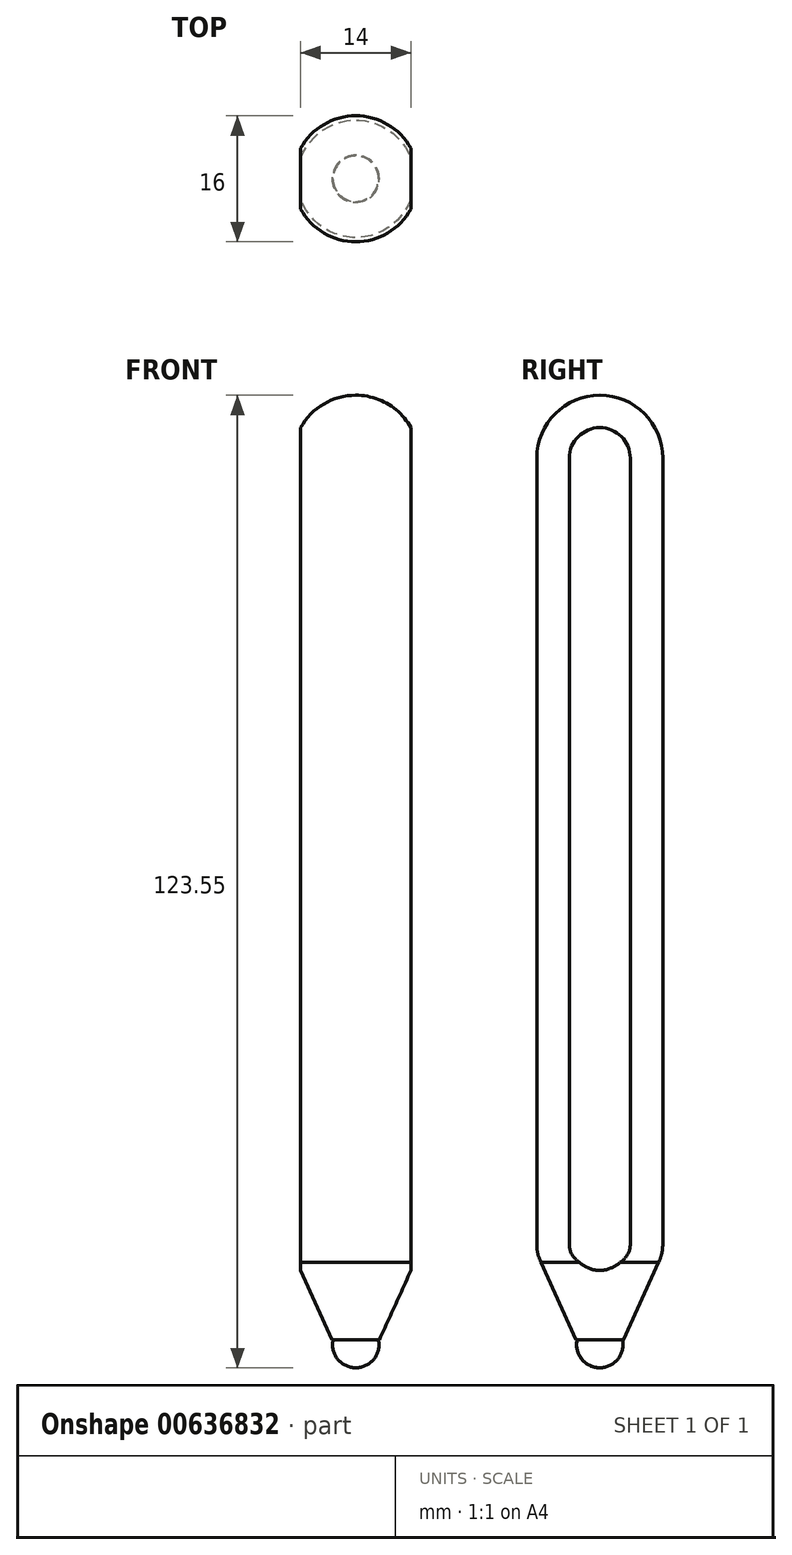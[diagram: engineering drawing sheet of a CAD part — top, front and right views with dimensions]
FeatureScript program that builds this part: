
annotation { "Feature Type Name" : "Feature", "Feature Type Description" : "" }
export const myFeature = defineFeature(function(context is Context, id is Id, definition is map)
    precondition{}
    {
        {
            var Q0;
            Q0=qCreatedBy(makeId("Top.planeOp"),FACE);
            var sketch = newSketch(context, id + "F0", { "sketchPlane" : qUnion([Q0])});
            skCircle(sketch, "E0", {"center": v(0, 0) * mm, "radius": 8 * mm});
            skSolve(sketch);
        }
        {
            var Q0;
            Q0=makeQuery(id+"F0.imprint","IMPRINT",FACE,{"disambiguationData":[TD([[makeQuery(id+"F0.imprint","IMPRINT",EDGE,{"derivedFrom":sQuery(id+"F0.wireOp",EDGE,"E0")}),1.0]])]});
            extrude(context, id + "F1", {"entities" : qUnion([Q0]), "depth" : 120 * mm, "offsetDistance" : 25 * mm});
        }
        {
            var Q0;
            Q0=makeQuery(id+"F1.opExtrude","CAP_FACE",FACE,{"disambiguationData":[OSD([sQuery(id+"F0.wireOp",EDGE,"E0")])],"isStart":false});
            fillet(context, id + "F2", {"entities" : qUnion([Q0]), "radius" : 8 * mm, "tangentPropagation" : true, "allowEdgeOverflow" : false});
        }
        {
            var Q0;
            Q0=makeQuery(id+"F1.opExtrude","CAP_FACE",FACE,{"disambiguationData":[OSD([sQuery(id+"F0.wireOp",EDGE,"E0")])],"isStart":true});
            chamfer(context, id + "F3", {"entities" : qUnion([Q0]), "chamferType" : ChamferType.TWO_OFFSETS, "width1" : 11 * mm, "oppositeDirection" : false, "width2" : 5 * mm, "tangentPropagation" : true});
        }
        {
            var Q0;
            Q0=qCreatedBy(makeId("Right.planeOp"),FACE);
            var sketch = newSketch(context, id + "F4", { "sketchPlane" : qUnion([Q0])});
            skArc(sketch, "E1", {"start": v(0, -3.55) * mm, "mid": v(2.95, -0.6) * mm, "end": v(0, 2.34) * mm});
            skLineSegment(sketch, "E2", {"start": v(0, 2.34) * mm, "end": v(0, -3.55) * mm});
            skSolve(sketch);
        }
        {
            var Q0;
            Q0=makeQuery(id+"F4.imprint","IMPRINT",FACE,{"disambiguationData":[TD([[makeQuery(id+"F4.imprint","IMPRINT",EDGE,{"derivedFrom":sQuery(id+"F4.wireOp",EDGE,"E1")}),1.0]])]});
            var Q1;
            Q1=sQuery(id+"F4.wireOp",EDGE,"E2");
            revolve(context, id + "F5", {"operationType" : NewBodyOperationType.ADD, "entities" : qUnion([Q0]), "axis" : qUnion([Q1]), "revolveType" : RevolveType.FULL});
        }
        {
            var Q0;
            Q0=qCreatedBy(makeId("Top.planeOp"),FACE);
            cPlane(context, id + "F6", {"entities" : qUnion([Q0]), "cplaneType" : CPlaneType.OFFSET, "offset" : 10 * mm, "oppositeDirection" : true, "width" : 150 * mm, "height" : 150 * mm});
        }
        {
            var Q0;
            Q0=qCreatedBy(id+"F6.planeOp",FACE);
            var sketch = newSketch(context, id + "F7", { "sketchPlane" : qUnion([Q0])});
            skLineSegment(sketch, "E3.bottom", {"start": v(-7, -12.5) * mm, "end": v(7, -12.5) * mm});
            skLineSegment(sketch, "E3.top", {"start": v(-7, 12.5) * mm, "end": v(7, 12.5) * mm});
            skLineSegment(sketch, "E3.left", {"start": v(-7, -12.5) * mm, "end": v(-7, 12.5) * mm});
            skLineSegment(sketch, "E3.right", {"start": v(7, -12.5) * mm, "end": v(7, 12.5) * mm});
            skPoint(sketch, "E3.middle", {"position": v(0, 0) * mm});
            skSolve(sketch);
        }
        {
            var Q0;
            {var subQ0=sQuery(id+"F0.wireOp",EDGE,"E0");Q0=makeQuery(id+"F3.opChamfer","BLEND_EDGE",EDGE,{"blendedFrom":[makeQuery(id+"F1.opExtrude","CAP_EDGE",EDGE,{"disambiguationData":[OSD([subQ0])],"isStart":true}),makeQuery(id+"F1.opExtrude","SWEPT_FACE",FACE,{"disambiguationData":[OSD([subQ0])]})],"blendedInto":[makeQuery(id+"F1.opExtrude","SWEPT_FACE",FACE,{"disambiguationData":[OSD([subQ0])]})]});}
            fillet(context, id + "F8", {"entities" : qUnion([Q0]), "radius" : 6 * mm, "tangentPropagation" : true, "rho" : .6, "crossSection" : FilletCrossSection.CONIC, "allowEdgeOverflow" : false});
        }
        {
            var Q0;
            Q0=makeQuery(id+"F7.imprint","IMPRINT",FACE,{"disambiguationData":[TD([[makeQuery(id+"F7.imprint","IMPRINT",EDGE,{"derivedFrom":sQuery(id+"F7.wireOp",EDGE,"E3.bottom")}),1.0]])]});
            extrude(context, id + "F9", {"entities" : qUnion([Q0]), "operationType" : NewBodyOperationType.INTERSECT, "endBound" : BoundingType.THROUGH_ALL, "depth" : 130 * mm, "offsetDistance" : 25 * mm});
        }
    });
